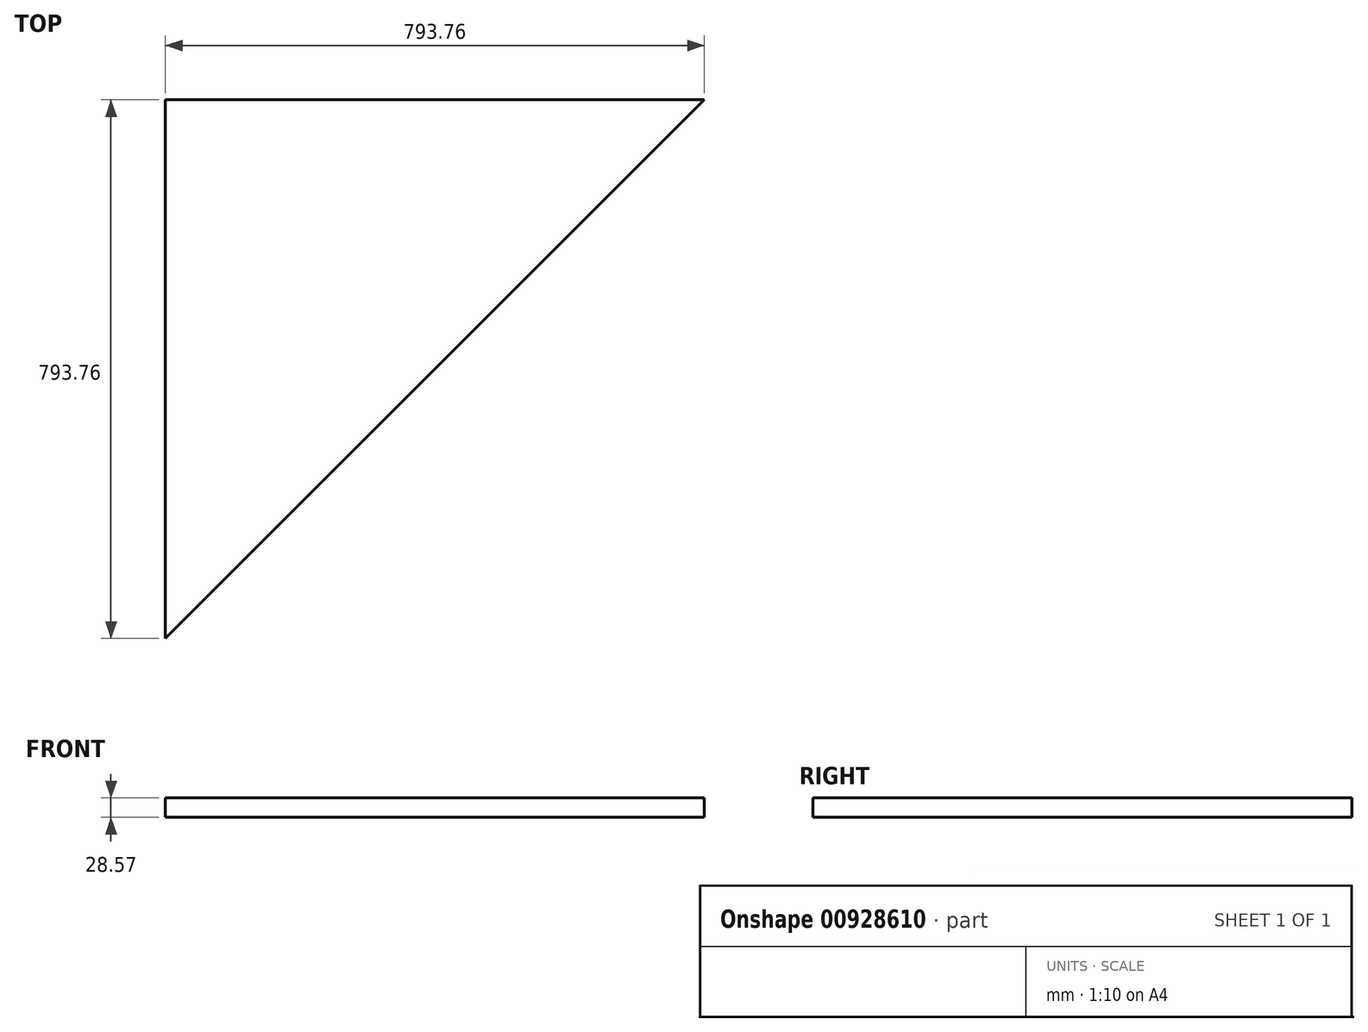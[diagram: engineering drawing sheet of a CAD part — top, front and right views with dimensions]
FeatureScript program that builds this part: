
annotation { "Feature Type Name" : "Feature", "Feature Type Description" : "" }
export const myFeature = defineFeature(function(context is Context, id is Id, definition is map)
    precondition{}
    {
        {
            var Q0;
            Q0=qCreatedBy(makeId("Top.planeOp"),FACE);
            var sketch = newSketch(context, id + "F0", { "sketchPlane" : qUnion([Q0])});
            skLineSegment(sketch, "E0.bottom", {"start": v(396.88, 396.88) * mm, "end": v(-396.88, 396.88) * mm});
            skLineSegment(sketch, "E0.top", {"start": v(396.88, -396.88) * mm, "end": v(-396.88, -396.88) * mm});
            skLineSegment(sketch, "E0.left", {"start": v(396.88, 396.88) * mm, "end": v(396.88, -396.88) * mm});
            skLineSegment(sketch, "E0.right", {"start": v(-396.88, 396.88) * mm, "end": v(-396.88, -396.88) * mm});
            skPoint(sketch, "E0.middle", {"position": v(0, 0) * mm});
            skLineSegment(sketch, "E1", {"start": v(-396.88, -396.87) * mm, "end": v(396.88, 396.88) * mm});
            skSolve(sketch);
        }
        {
            var Q0;
            Q0=makeQuery(id+"F0.imprint","IMPRINT",FACE,{"disambiguationData":[TD([[makeQuery(id+"F0.imprint","IMPRINT",EDGE,{"derivedFrom":sQuery(id+"F0.wireOp",EDGE,"E0.bottom")}),1.0]])]});
            extrude(context, id + "F1", {"entities" : qUnion([Q0]), "depth" : 28.57 * mm, "offsetDistance" : 25.4 * mm});
        }
    });
